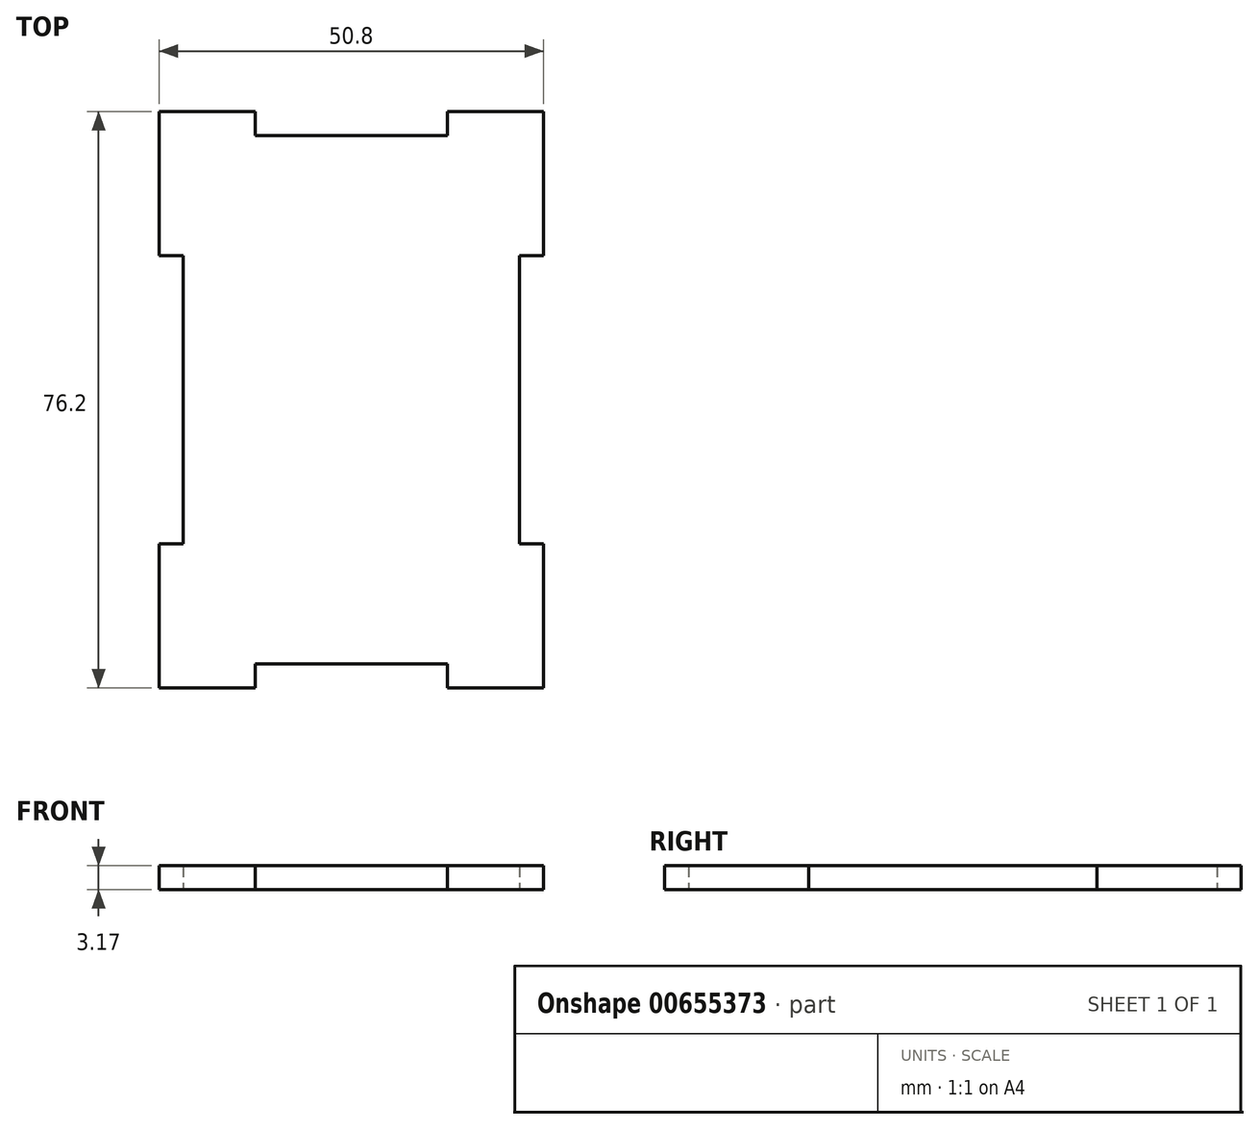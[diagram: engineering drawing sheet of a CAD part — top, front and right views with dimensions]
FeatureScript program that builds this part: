
annotation { "Feature Type Name" : "Feature", "Feature Type Description" : "" }
export const myFeature = defineFeature(function(context is Context, id is Id, definition is map)
    precondition{}
    {
        {
            var Q0;
            Q0=qCreatedBy(makeId("Top.planeOp"),FACE);
            var sketch = newSketch(context, id + "F0", { "sketchPlane" : qUnion([Q0])});
            skLineSegment(sketch, "E0.bottom", {"start": v(25.36, 36.95) * mm, "end": v(-25.44, 36.95) * mm});
            skLineSegment(sketch, "E0.top", {"start": v(25.36, -39.25) * mm, "end": v(-25.44, -39.25) * mm});
            skLineSegment(sketch, "E0.left", {"start": v(25.36, 36.95) * mm, "end": v(25.36, -39.25) * mm});
            skLineSegment(sketch, "E0.right", {"start": v(-25.44, 36.95) * mm, "end": v(-25.44, -39.25) * mm});
            skPoint(sketch, "E0.middle", {"position": v(-0.04, -1.15) * mm});
            skLineSegment(sketch, "E1.bottom", {"start": v(12.66, 40.12) * mm, "end": v(-12.74, 40.12) * mm});
            skLineSegment(sketch, "E1.top", {"start": v(12.66, 33.77) * mm, "end": v(-12.74, 33.77) * mm});
            skLineSegment(sketch, "E1.left", {"start": v(12.66, 40.12) * mm, "end": v(12.66, 33.77) * mm});
            skLineSegment(sketch, "E1.right", {"start": v(-12.74, 40.12) * mm, "end": v(-12.74, 33.77) * mm});
            skPoint(sketch, "E1.middle", {"position": v(-0.04, 36.95) * mm});
            skLineSegment(sketch, "E2.bottom", {"start": v(28.53, 17.9) * mm, "end": v(22.18, 17.9) * mm});
            skLineSegment(sketch, "E2.top", {"start": v(28.53, -20.2) * mm, "end": v(22.18, -20.2) * mm});
            skLineSegment(sketch, "E2.left", {"start": v(28.53, 17.9) * mm, "end": v(28.53, -20.2) * mm});
            skLineSegment(sketch, "E2.right", {"start": v(22.18, 17.9) * mm, "end": v(22.18, -20.2) * mm});
            skPoint(sketch, "E2.middle", {"position": v(25.36, -1.15) * mm});
            skLineSegment(sketch, "E3.MirrorCS", {"start": v(-28.62, 17.9) * mm, "end": v(-22.27, 17.9) * mm});
            skLineSegment(sketch, "E4.MirrorCS", {"start": v(-22.27, 17.9) * mm, "end": v(-22.27, -20.2) * mm});
            skLineSegment(sketch, "E5.MirrorCS", {"start": v(-28.62, 17.9) * mm, "end": v(-28.62, -20.2) * mm});
            skLineSegment(sketch, "E6.MirrorCS", {"start": v(-28.62, -20.2) * mm, "end": v(-22.27, -20.2) * mm});
            skLineSegment(sketch, "E7.MirrorCS", {"start": v(12.66, -36.08) * mm, "end": v(-12.74, -36.08) * mm});
            skLineSegment(sketch, "E8.MirrorCS", {"start": v(12.66, -42.43) * mm, "end": v(-12.74, -42.43) * mm});
            skLineSegment(sketch, "E9.MirrorCS", {"start": v(12.66, -42.43) * mm, "end": v(12.66, -36.08) * mm});
            skLineSegment(sketch, "E10.MirrorCS", {"start": v(-12.74, -42.43) * mm, "end": v(-12.74, -36.08) * mm});
            skSolve(sketch);
        }
        {
            var Q0;
            {var subQ1=sQuery(id+"F0.wireOp",EDGE,"E1.top");Q0=makeQuery(id+"F0.imprint","IMPRINT",FACE,{"disambiguationData":[TD([[makeQuery(id+"F0.imprint","IMPRINT",EDGE,{"derivedFrom":subQ1}),1.0]])]});}
            extrude(context, id + "F1", {"entities" : qUnion([Q0]), "depth" : 3.17 * mm, "offsetDistance" : 25.4 * mm});
        }
    });
